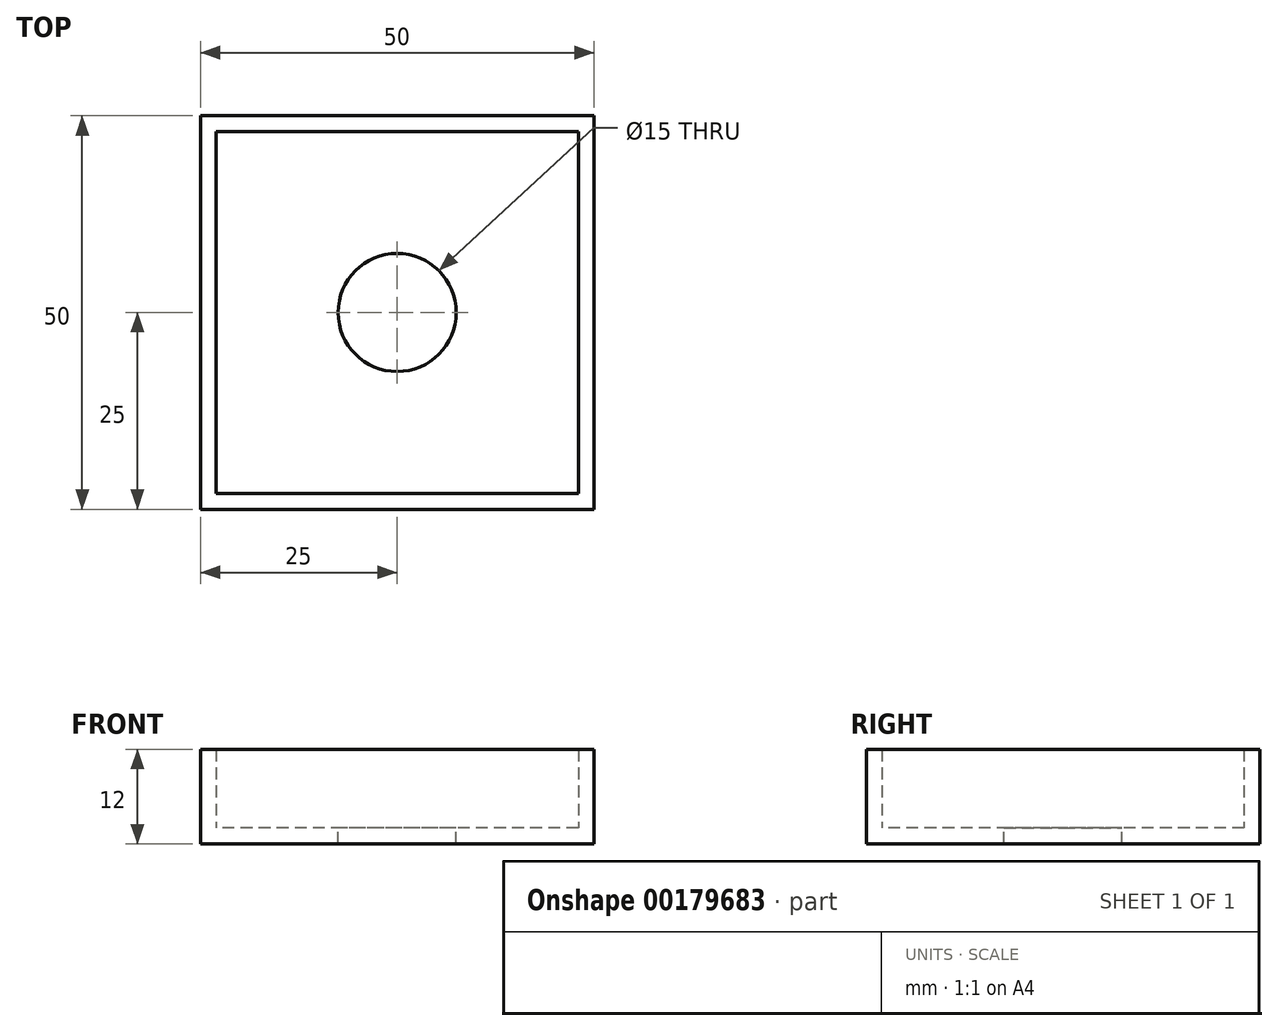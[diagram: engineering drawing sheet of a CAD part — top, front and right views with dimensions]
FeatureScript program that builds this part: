
annotation { "Feature Type Name" : "Feature", "Feature Type Description" : "" }
export const myFeature = defineFeature(function(context is Context, id is Id, definition is map)
    precondition{}
    {
        {
            var Q0;
            Q0=qCreatedBy(makeId("Top.planeOp"),FACE);
            var sketch = newSketch(context, id + "F0", { "sketchPlane" : qUnion([Q0])});
            skLineSegment(sketch, "E0.bottom", {"start": v(25, 25) * mm, "end": v(-25, 25) * mm});
            skLineSegment(sketch, "E0.top", {"start": v(25, -25) * mm, "end": v(-25, -25) * mm});
            skLineSegment(sketch, "E0.left", {"start": v(25, 25) * mm, "end": v(25, -25) * mm});
            skLineSegment(sketch, "E0.right", {"start": v(-25, 25) * mm, "end": v(-25, -25) * mm});
            skPoint(sketch, "E0.middle", {"position": v(0, 0) * mm});
            skCircle(sketch, "E1", {"center": v(0, 0) * mm, "radius": 7.5 * mm});
            skSolve(sketch);
        }
        {
            var Q0;
            Q0=makeQuery(id+"F0.imprint","IMPRINT",FACE,{"disambiguationData":[TD([[makeQuery(id+"F0.imprint","IMPRINT",EDGE,{"derivedFrom":sQuery(id+"F0.wireOp",EDGE,"E0.bottom")}),1.0]])]});
            var sketch = newSketch(context, id + "F1", { "sketchPlane" : qUnion([Q0])});
            skLineSegment(sketch, "E2.bottom", {"start": v(23, 23) * mm, "end": v(-23, 23) * mm});
            skLineSegment(sketch, "E2.top", {"start": v(23, -23) * mm, "end": v(-23, -23) * mm});
            skLineSegment(sketch, "E2.left", {"start": v(23, 23) * mm, "end": v(23, -23) * mm});
            skLineSegment(sketch, "E2.right", {"start": v(-23, 23) * mm, "end": v(-23, -23) * mm});
            skPoint(sketch, "E2.middle", {"position": v(0, 0) * mm});
            skSolve(sketch);
        }
        {
            var Q0;
            Q0=makeQuery(id+"F0.imprint","IMPRINT",FACE,{"disambiguationData":[TD([[makeQuery(id+"F0.imprint","IMPRINT",EDGE,{"derivedFrom":sQuery(id+"F0.wireOp",EDGE,"E0.bottom")}),1.0]])]});
            extrude(context, id + "F2", {"entities" : qUnion([Q0]), "oppositeDirection" : true, "depth" : 2 * mm});
        }
        {
            var Q0;
            Q0=makeQuery(id+"F1.imprint","IMPRINT",FACE,{"disambiguationData":[TD([[makeQuery(id+"F1.imprint","IMPRINT",EDGE,{"derivedFrom":sQuery(id+"F1.wireOp",EDGE,"E2.bottom")}),-1.0]])]});
            extrude(context, id + "F3", {"entities" : qUnion([Q0]), "operationType" : NewBodyOperationType.ADD, "depth" : 10 * mm});
        }
    });
